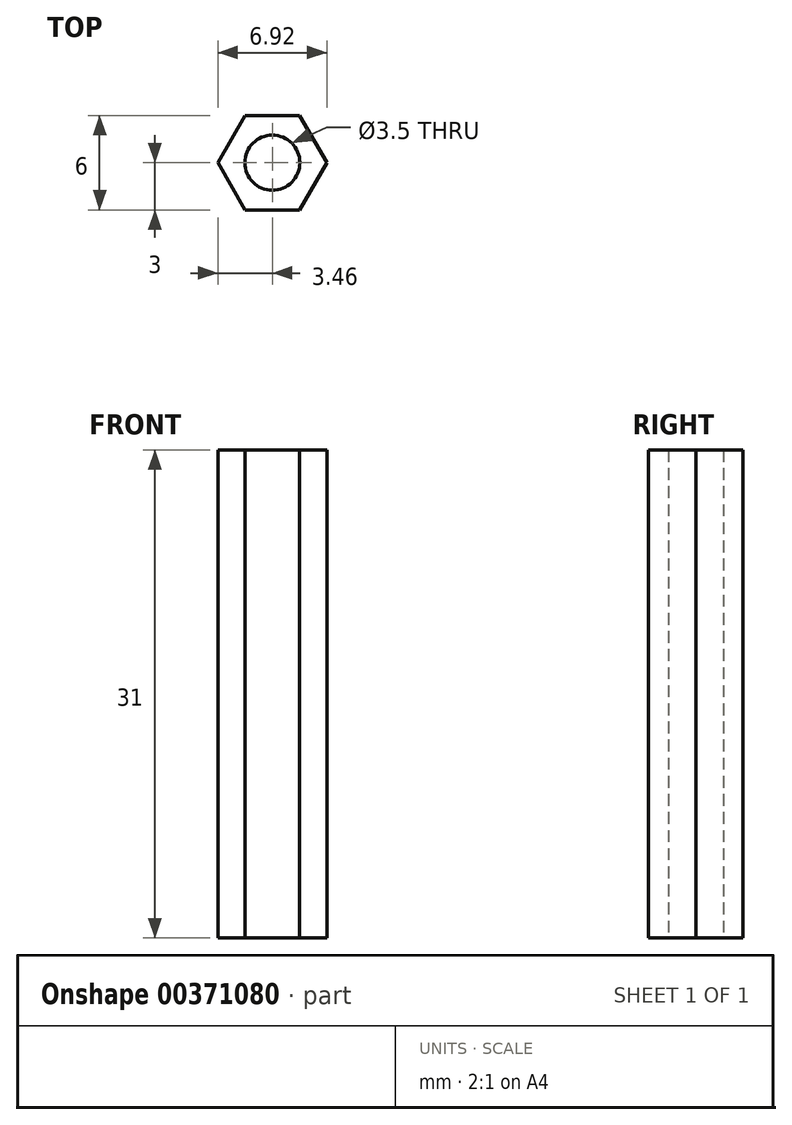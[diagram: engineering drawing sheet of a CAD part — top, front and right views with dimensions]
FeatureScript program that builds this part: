
annotation { "Feature Type Name" : "Feature", "Feature Type Description" : "" }
export const myFeature = defineFeature(function(context is Context, id is Id, definition is map)
    precondition{}
    {
        {
            var Q0;
            Q0=qCreatedBy(makeId("Top.planeOp"),FACE);
            var sketch = newSketch(context, id + "F0", { "sketchPlane" : qUnion([Q0])});
            skCircle(sketch, "E0", {"center": v(0, 0) * mm, "radius": 1.75 * mm});
            skCircle(sketch, "E1.cCircle", {"center": v(0, 0) * mm, "radius": 3 * mm, "construction": true});
            skLineSegment(sketch, "E1.0", {"start": v(-1.73, 3) * mm, "end": v(1.73, 3) * mm});
            skLineSegment(sketch, "E1.1", {"start": v(1.73, 3) * mm, "end": v(3.46, 0) * mm});
            skLineSegment(sketch, "E1.2", {"start": v(3.46, 0) * mm, "end": v(1.73, -3) * mm});
            skLineSegment(sketch, "E1.3", {"start": v(1.73, -3) * mm, "end": v(-1.73, -3) * mm});
            skLineSegment(sketch, "E1.4", {"start": v(-1.73, -3) * mm, "end": v(-3.46, 0) * mm});
            skLineSegment(sketch, "E1.5", {"start": v(-3.46, 0) * mm, "end": v(-1.73, 3) * mm});
            skPoint(sketch, "E1.0.midPoint", {"position": v(0, 3) * mm});
            skSolve(sketch);
        }
        {
            var Q0;
            Q0=qSketchRegion(id+"F0",true);
            extrude(context, id + "F1", {"entities" : qUnion([Q0]), "endBound" : BoundingType.SYMMETRIC, "depth" : 31 * mm});
        }
    });
